# Revit family: 4070756+4070746+4070771 Feilo Sylvania Lighting Fixture CURSUS 876MM 653LM OVAL LED 4K with CONTINUOUS WALL HOUSING with 70MM WALL BRACKET
name_source: partatom
category: Lighting Fixtures
revit_build: Autodesk Revit 2017 (Build: 20190507_1515(x64)
units: mm (PartAtom-declared; Revit-internal decimal feet)

## family parameters
Cut with Voids When Loaded = Yes
Host = Face
Light Source = No
OmniClass Number = 23.80.70.14
OmniClass Title = Luminaries for External Lighting
Part Type = Normal
Room Calculation Point = No
Round Connector Dimension = Use Diameter
Shared = No

## types (1)
- 4070756 CURSUS 876MM 653LM OVAL LED 4K
    AccessoryMaterial = Diffuser-Sylvania-Glow
    Apparent Load = 14 VA
    Assembly Code = D5020200
    AssetType = Fixed
    BodyMaterial = Body-Sylvania-Gray
    BracketC = 22 mm  [stored 0.0721785 ft]
    BracketD = 21 mm
    BracketDistance = 745 mm  [stored 2.44423 ft]
    BracketEndReduction = 25 mm  [stored 0.082021 ft]
    BracketExtension = 70 mm  [stored 0.229659 ft]
    BracketFlange = 11 mm  [stored 0.0360892 ft]
    BracketHeight = 55 mm  [stored 0.180446 ft]
    BracketHeightEnd = 32 mm  [stored 0.104987 ft]
    BracketThickness = 2 mm  [stored 0.00656168 ft]
    BracketWidth = 24 mm  [stored 0.0787402 ft]
    ClassificationName = Uniclass2015
    ClassificationValue = EF_70_80
    Cost = 0 $
    Default Elevation = 1219 mm
    Description = LED Exterior Lighting Recessed Surface Mounted Linear Fixture, Natural anodised extruded aluminium structure. Die-cast aluminium end caps. Installation kit with harmonic steel springs., 653 lm, 13,5W,  48lm/W, 4000K, CRI80+,non dimmable,IP67, IK07, (HxWxD) 876x50x30mm, 3 step Mac Adam Ellipse, 1.7kg,, Classe III, 21-25V-DC, energy class : A++, A+, A
    DiffuserMaterial = Diffuser-Sylvania-Glow
    DocumentationLiterature = http://www.sylvania-lighting.com
    DurationUnit = hours
    ElectricShockClassification = Class III
    ExpectedLife = 50000
    IfcExportAs = IfcLightFixtureType
    IfcExportType = IfcLightFixtureType
    ImpactProtectionIndex = IK07
    IngressProtection = IP67
    InputVoltage = 24V DC
    Keynote = 16500
    Lamp = LED
    LampColourRenderingIndex = 80
    LampColourTemperature = 4000 K
    LampNominalLuminous = 653 lm
    LampsType = LED
    LightOutputRatio = 100
    LuminousEfficacy = 48.37 lm/W
    Manufacturer = Feilo Sylvania
    ManufacturerName = Feilo Sylvania
    Material = natural anodised extruded aluminium structure housing, optical system with pmma lenses diffuser
    Model = CURSUS 876MM 653LM OVAL LED 4K
    ModelNumber = 4070756
    ModelReference = CURSUS 876MM 653LM OVAL LED 4K
    Name = CURSUS 876MM 653LM OVAL LED 4K
    NominalDepth = 30 mm  [stored 0.0984252 ft]
    NominalHeight = 50 mm  [stored 0.164042 ft]
    NominalLength = 876 mm  [stored 2.87402 ft]
    PowerConsumption = 13.5 W
    PowerFactor = 0
    ReflectorMaterial = <By Category>
    Type Image = <None>
    TypeFixture_FEILO = CURSUS with CONTINUOUS WALL HOUSING : CURSUS 876MM 653LM OVAL LED 4K
    TypeName = CURSUS 876MM 653LM OVAL LED 4K
    URL = http://www.sylvania-lighting.com
    Voltage = 24 V
    Weight = 1.7 kg

note: [stored X ft] marks values corroborated as IEEE doubles in the binary element streams (Revit-internal decimal feet)

## geometry (parser evidence)
native form markers: Sweep x6
no freeform markers — native parametric forms only
